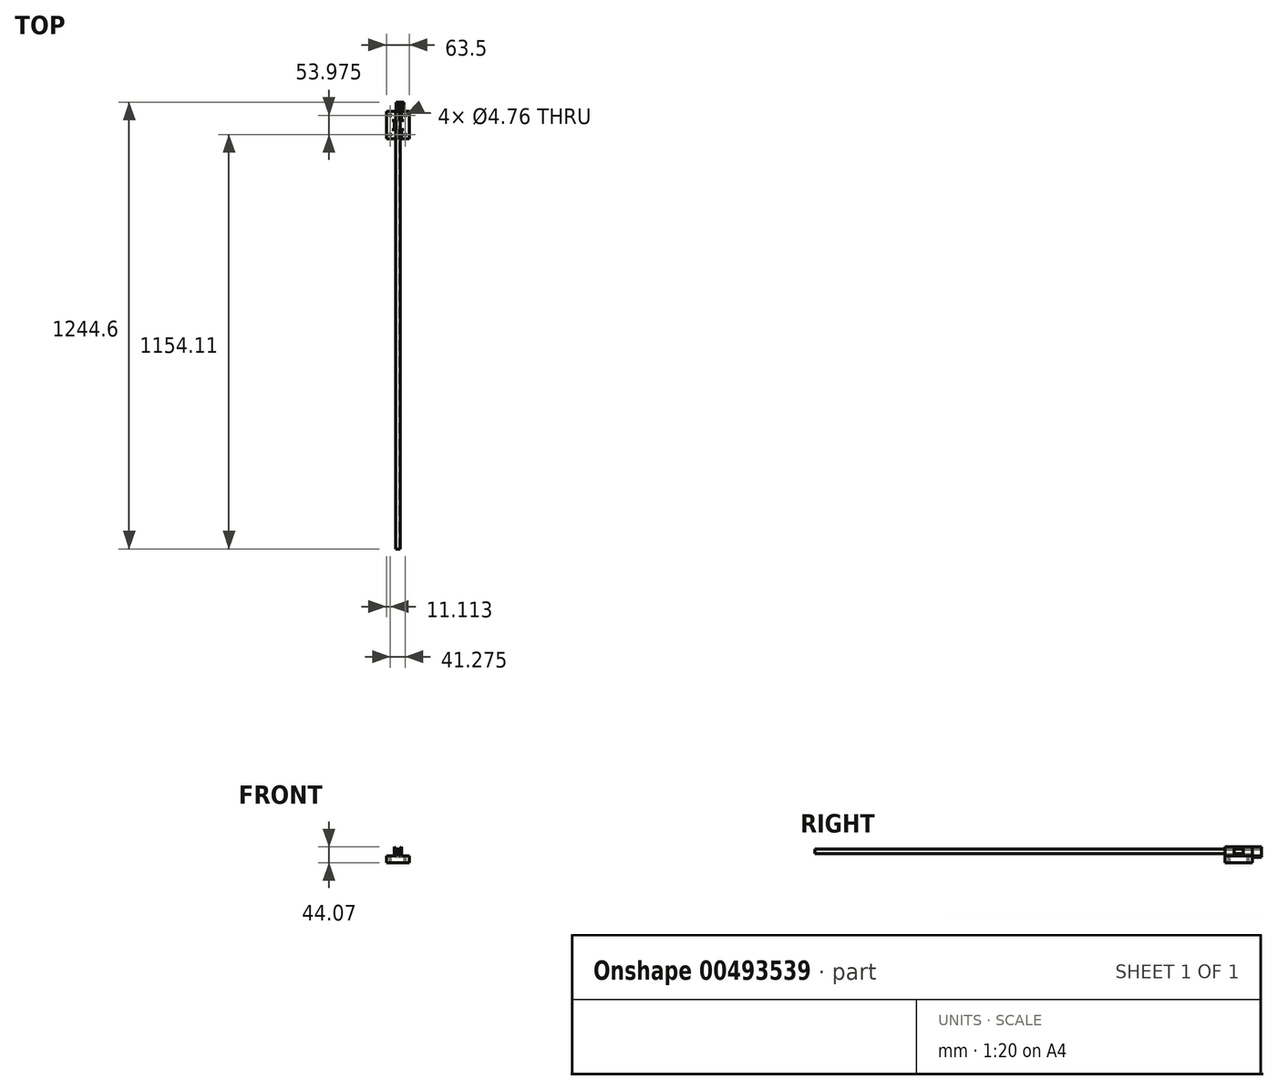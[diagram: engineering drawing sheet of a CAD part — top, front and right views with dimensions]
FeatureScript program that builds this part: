
annotation { "Feature Type Name" : "Feature", "Feature Type Description" : "" }
export const myFeature = defineFeature(function(context is Context, id is Id, definition is map)
    precondition{}
    {
        {
            var Q0;
            Q0=qCreatedBy(makeId("Front.planeOp"),FACE);
            var sketch = newSketch(context, id + "F0", { "sketchPlane" : qUnion([Q0])});
            skLineSegment(sketch, "E0", {"start": v(-6.35, -6.35) * mm, "end": v(-6.35, 6.35) * mm});
            skLineSegment(sketch, "E1", {"start": v(-6.35, 6.35) * mm, "end": v(6.35, 6.35) * mm});
            skLineSegment(sketch, "E2", {"start": v(6.35, 6.35) * mm, "end": v(6.35, -6.35) * mm});
            skLineSegment(sketch, "E3.0", {"start": v(4.76, 4.76) * mm, "end": v(4.76, -6.35) * mm});
            skLineSegment(sketch, "E3.1", {"start": v(-4.76, 4.76) * mm, "end": v(4.76, 4.76) * mm});
            skLineSegment(sketch, "E3.2", {"start": v(-4.76, -6.35) * mm, "end": v(-4.76, 4.76) * mm});
            skLineSegment(sketch, "E4", {"start": v(-6.35, -6.35) * mm, "end": v(-4.76, -6.35) * mm});
            skLineSegment(sketch, "E5", {"start": v(4.76, -6.35) * mm, "end": v(6.35, -6.35) * mm});
            skLineSegment(sketch, "E6.bottom", {"start": v(-4.75, 4.5) * mm, "end": v(4.75, 4.5) * mm});
            skLineSegment(sketch, "E6.left", {"start": v(-4.75, 4.5) * mm, "end": v(-4.75, -12.7) * mm});
            skLineSegment(sketch, "E6.right", {"start": v(4.75, 4.5) * mm, "end": v(4.75, -12.7) * mm});
            skLineSegment(sketch, "E7.bottom", {"start": v(-31.75, -12.7) * mm, "end": v(-16.5, -12.7) * mm});
            skLineSegment(sketch, "E7.left", {"start": v(-31.75, -12.7) * mm, "end": v(-31.75, -31.75) * mm});
            skLineSegment(sketch, "E7.right", {"start": v(31.75, -12.7) * mm, "end": v(31.75, -31.75) * mm});
            skLineSegment(sketch, "E8.trimOffspring", {"start": v(16.5, -12.7) * mm, "end": v(31.75, -12.7) * mm});
            skPoint(sketch, "E9.visualSharp", {"position": v(-4.75, -12.7) * mm});
            skPoint(sketch, "E10.visualSharp", {"position": v(4.75, -12.7) * mm});
            skLineSegment(sketch, "E11", {"start": v(-10.16, -6.35) * mm, "end": v(-10.16, 12.32) * mm});
            skLineSegment(sketch, "E12", {"start": v(-10.16, 12.32) * mm, "end": v(-4.44, 6.6) * mm});
            skLineSegment(sketch, "E13", {"start": v(-4.44, 6.6) * mm, "end": v(-6.98, 6.6) * mm});
            skLineSegment(sketch, "E14", {"start": v(-6.99, 6.6) * mm, "end": v(-6.98, -12.7) * mm});
            skLineSegment(sketch, "E15", {"start": v(-6.99, -12.7) * mm, "end": v(-4.75, -12.7) * mm});
            skLineSegment(sketch, "E16", {"start": v(4.75, -12.7) * mm, "end": v(6.99, -12.7) * mm});
            skLineSegment(sketch, "E17", {"start": v(6.99, -12.7) * mm, "end": v(6.99, 6.6) * mm});
            skLineSegment(sketch, "E18", {"start": v(6.99, 6.6) * mm, "end": v(4.44, 6.6) * mm});
            skLineSegment(sketch, "E19", {"start": v(4.44, 6.6) * mm, "end": v(10.16, 12.32) * mm});
            skLineSegment(sketch, "E20", {"start": v(10.16, 12.32) * mm, "end": v(10.16, -6.35) * mm});
            skPoint(sketch, "E21.visualSharp", {"position": v(-10.16, -12.7) * mm});
            skArc(sketch, "E21.filletArc", {"start": v(-16.5, -12.7) * mm, "mid": v(-12.02, -10.84) * mm, "end": v(-10.16, -6.35) * mm});
            skPoint(sketch, "E22.visualSharp", {"position": v(10.16, -12.7) * mm});
            skArc(sketch, "E22.filletArc", {"start": v(10.16, -6.35) * mm, "mid": v(12.02, -10.84) * mm, "end": v(16.5, -12.7) * mm});
            skLineSegment(sketch, "E23", {"start": v(-31.75, -31.75) * mm, "end": v(31.75, -31.75) * mm});
            skSolve(sketch);
        }
        {
            var Q0;
            Q0=makeQuery(id+"F0.imprint","IMPRINT",FACE,{"disambiguationData":[TD([[makeQuery(id+"F0.imprint","IMPRINT",EDGE,{"derivedFrom":sQuery(id+"F0.wireOp",EDGE,"E6.bottom")}),-1.0]])]});
            extrude(context, id + "F1", {"entities" : qUnion([Q0]), "depth" : 76.2 * mm, "offsetDistance" : 25.4 * mm});
        }
        {
            var Q0;
            Q0=makeQuery(id+"F1.opExtrude","SWEPT_FACE",FACE,{"disambiguationData":[OSD([sQuery(id+"F0.wireOp",EDGE,"E20")])]});
            var sketch = newSketch(context, id + "F2", { "sketchPlane" : qUnion([Q0])});
            skLineSegment(sketch, "E24.bottom", {"start": v(-50.8, 12.32) * mm, "end": v(-25.4, 12.32) * mm});
            skLineSegment(sketch, "E24.top", {"start": v(-50.8, -12.7) * mm, "end": v(-25.4, -12.7) * mm});
            skLineSegment(sketch, "E24.left", {"start": v(-50.8, 12.32) * mm, "end": v(-50.8, -12.7) * mm});
            skLineSegment(sketch, "E24.right", {"start": v(-25.4, 12.32) * mm, "end": v(-25.4, -12.7) * mm});
            skSolve(sketch);
        }
        {
            var Q0;
            Q0 = qSketchRegion(id + "F2", true);
            extrude(context, id + "F3", {"entities" : qUnion([Q0]), "operationType" : NewBodyOperationType.REMOVE, "endBound" : BoundingType.UP_TO_NEXT, "oppositeDirection" : true, "depth" : 25.4 * mm, "offsetDistance" : 25.4 * mm});
        }
        {
            var Q0;
            Q0=makeQuery(id+"F1.opExtrude","SWEPT_FACE",FACE,{"disambiguationData":[OSD([sQuery(id+"F0.wireOp",EDGE,"E11")])]});
            var sketch = newSketch(context, id + "F4", { "sketchPlane" : qUnion([Q0])});
            skLineSegment(sketch, "E25.bottom", {"start": v(0, 12.32) * mm, "end": v(25.4, 12.32) * mm});
            skLineSegment(sketch, "E25.top", {"start": v(0, -12.7) * mm, "end": v(25.4, -12.7) * mm});
            skLineSegment(sketch, "E25.left", {"start": v(0, 12.32) * mm, "end": v(0, -12.7) * mm});
            skLineSegment(sketch, "E25.right", {"start": v(25.4, 12.32) * mm, "end": v(25.4, -12.7) * mm});
            skLineSegment(sketch, "E26.bottom", {"start": v(76.2, 12.32) * mm, "end": v(50.8, 12.32) * mm});
            skLineSegment(sketch, "E26.top", {"start": v(76.2, -12.7) * mm, "end": v(50.8, -12.7) * mm});
            skLineSegment(sketch, "E26.left", {"start": v(76.2, 12.32) * mm, "end": v(76.2, -12.7) * mm});
            skLineSegment(sketch, "E26.right", {"start": v(50.8, 12.32) * mm, "end": v(50.8, -12.7) * mm});
            skSolve(sketch);
        }
        {
            var Q0;
            Q0 = qSketchRegion(id + "F4", true);
            extrude(context, id + "F5", {"entities" : qUnion([Q0]), "operationType" : NewBodyOperationType.REMOVE, "endBound" : BoundingType.UP_TO_NEXT, "oppositeDirection" : true, "depth" : 25.4 * mm, "offsetDistance" : 25.4 * mm});
        }
        {
            var Q0;
            Q0 = qSketchRegion(id + "F4", true);
            extrude(context, id + "F6", {"entities" : qUnion([Q0]), "operationType" : NewBodyOperationType.REMOVE, "depth" : 25.4 * mm, "offsetDistance" : 25.4 * mm});
        }
        {
            var Q0;
            Q0 = qSketchRegion(id + "F2", true);
            extrude(context, id + "F7", {"entities" : qUnion([Q0]), "operationType" : NewBodyOperationType.REMOVE, "depth" : 25.4 * mm, "offsetDistance" : 25.4 * mm});
        }
        {
            var Q0;
            Q0=makeQuery(id+"F0.imprint","IMPRINT",FACE,{"disambiguationData":[TD([[makeQuery(id+"F0.imprint","IMPRINT",EDGE,{"derivedFrom":sQuery(id+"F0.wireOp",EDGE,"E0")}),-1.0]])]});
            extrude(context, id + "F8", {"entities" : qUnion([Q0]), "depth" : 1219.2 * mm, "offsetDistance" : 25.4 * mm});
        }
        {
            var Q0;
            Q0=qCreatedBy(makeId("Top.planeOp"),FACE);
            var sketch = newSketch(context, id + "F9", { "sketchPlane" : qUnion([Q0])});
            skCircle(sketch, "E27", {"center": v(-20.64, -11.11) * mm, "radius": 2.38 * mm});
            skCircle(sketch, "E28", {"center": v(-20.64, -65.09) * mm, "radius": 2.38 * mm});
            skCircle(sketch, "E29", {"center": v(20.64, -11.11) * mm, "radius": 2.38 * mm});
            skCircle(sketch, "E30", {"center": v(20.64, -65.09) * mm, "radius": 2.38 * mm});
            skSolve(sketch);
        }
        {
            var Q0;
            Q0 = qSketchRegion(id + "F9", true);
            extrude(context, id + "F10", {"entities" : qUnion([Q0]), "operationType" : NewBodyOperationType.REMOVE, "endBound" : BoundingType.THROUGH_ALL, "oppositeDirection" : true, "depth" : 25.4 * mm, "offsetDistance" : 25.4 * mm});
        }
        {
            var Q0;
            Q0=qCreatedBy(makeId("Front.planeOp"),FACE);
            var sketch = newSketch(context, id + "F11", { "sketchPlane" : qUnion([Q0])});
            skLineSegment(sketch, "E31.bottom", {"start": v(16.51, -12.7) * mm, "end": v(16.51, -12.7) * mm});
            skLineSegment(sketch, "E31.top", {"start": v(16.51, -15.87) * mm, "end": v(-4.75, -15.87) * mm});
            skLineSegment(sketch, "E31.left", {"start": v(16.51, -12.7) * mm, "end": v(16.51, -15.87) * mm});
            skLineSegment(sketch, "E32", {"start": v(10.16, -6.35) * mm, "end": v(10.16, 12.32) * mm});
            skLineSegment(sketch, "E33", {"start": v(10.16, 12.32) * mm, "end": v(4.44, 6.6) * mm});
            skLineSegment(sketch, "E34", {"start": v(4.44, 6.6) * mm, "end": v(6.98, 6.6) * mm});
            skLineSegment(sketch, "E35", {"start": v(6.98, 6.6) * mm, "end": v(6.99, -12.7) * mm});
            skLineSegment(sketch, "E36.trimOffspring", {"start": v(6.99, -12.7) * mm, "end": v(4.75, -12.7) * mm});
            skPoint(sketch, "E37.visualSharp", {"position": v(10.16, -12.7) * mm});
            skArc(sketch, "E37.filletArc", {"start": v(10.16, -6.35) * mm, "mid": v(12.02, -10.84) * mm, "end": v(16.51, -12.7) * mm});
            skLineSegment(sketch, "E38", {"start": v(4.75, -12.7) * mm, "end": v(4.75, 4.5) * mm});
            skLineSegment(sketch, "E39", {"start": v(4.75, 4.5) * mm, "end": v(-4.75, 4.5) * mm});
            skLineSegment(sketch, "E40", {"start": v(-4.75, 4.5) * mm, "end": v(-4.75, -15.87) * mm});
            skSolve(sketch);
        }
        {
            var Q0;
            Q0 = qSketchRegion(id + "F11", true);
            extrude(context, id + "F12", {"entities" : qUnion([Q0]), "oppositeDirection" : true, "depth" : 25.4 * mm, "offsetDistance" : 25.4 * mm});
        }
    });
